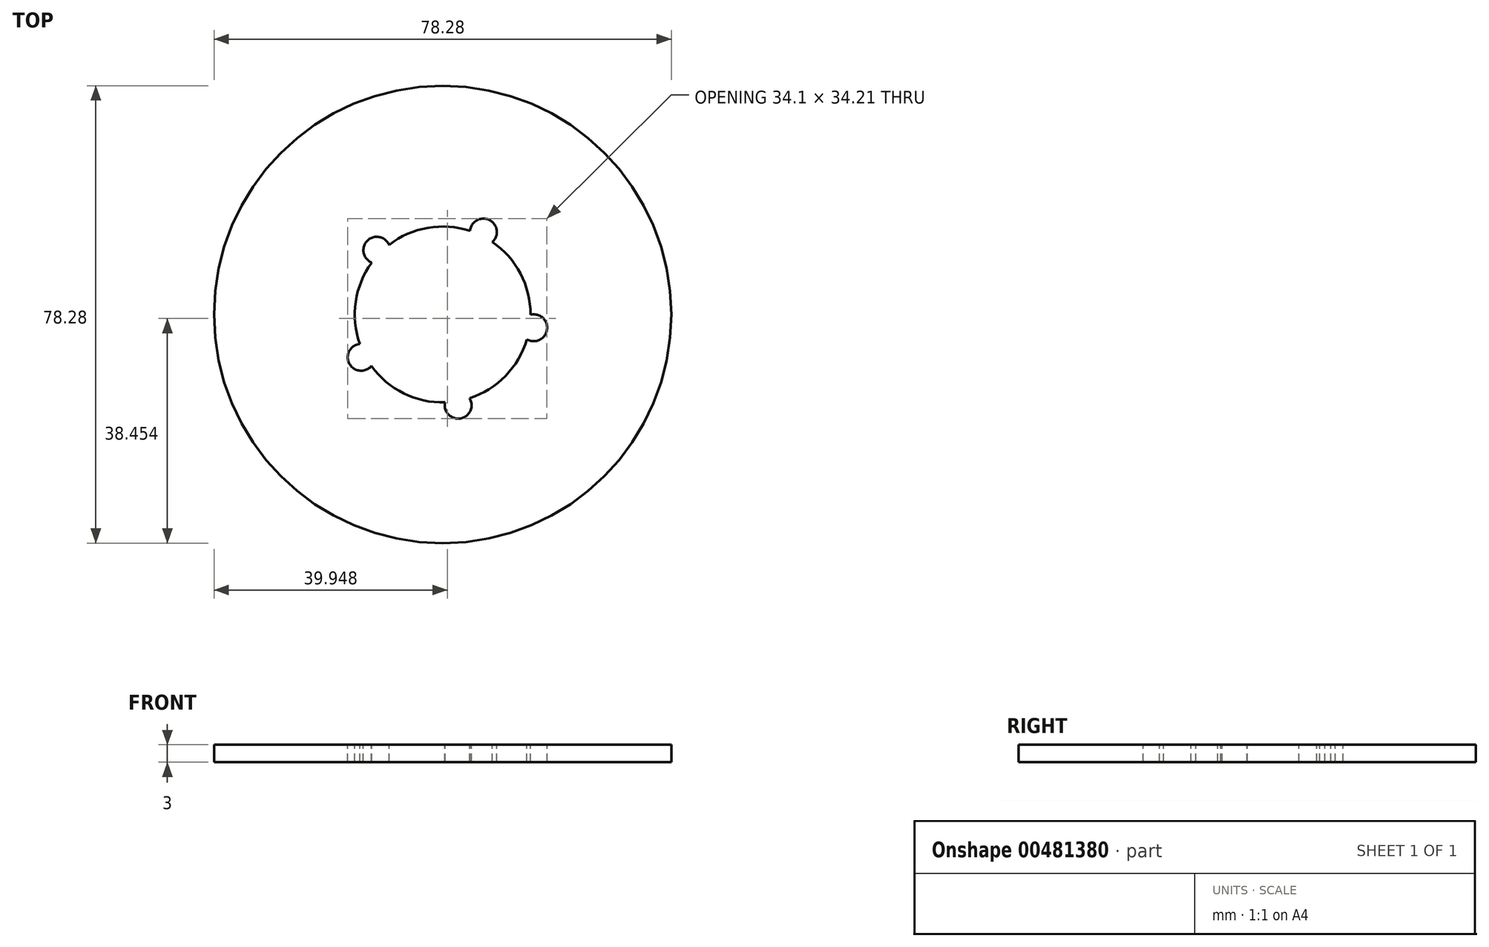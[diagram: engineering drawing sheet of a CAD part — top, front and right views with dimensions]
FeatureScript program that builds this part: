
annotation { "Feature Type Name" : "Feature", "Feature Type Description" : "" }
export const myFeature = defineFeature(function(context is Context, id is Id, definition is map)
    precondition{}
    {
        {
            var Q0;
            Q0=qCreatedBy(makeId("Top.planeOp"),FACE);
            var sketch = newSketch(context, id + "F0", { "sketchPlane" : qUnion([Q0])});
            skCircle(sketch, "E0", {"center": v(0, 0) * mm, "radius": 39.14 * mm});
            skSolve(sketch);
        }
        {
            var Q0;
            Q0 = qSketchRegion(id + "F0", true);
            extrude(context, id + "F1", {"entities" : qUnion([Q0]), "depth" : 3 * mm});
        }
        {
            var Q0;
            Q0=makeQuery(id+"F1.opExtrude","CAP_FACE",FACE,{"disambiguationData":[OSD([sQuery(id+"F0.wireOp",EDGE,"E0")])],"isStart":false});
            var sketch = newSketch(context, id + "F2", { "sketchPlane" : qUnion([Q0])});
            skCircle(sketch, "E1", {"center": v(0, 0) * mm, "radius": 15.05 * mm});
            skSolve(sketch);
        }
        {
            var Q0;
            Q0 = qSketchRegion(id + "F2", true);
            extrude(context, id + "F3", {"entities" : qUnion([Q0]), "operationType" : NewBodyOperationType.REMOVE, "oppositeDirection" : true, "depth" : 3 * mm});
        }
        {
            var Q0;
            Q0=makeQuery(id+"F1.opExtrude","CAP_FACE",FACE,{"disambiguationData":[OSD([sQuery(id+"F0.wireOp",EDGE,"E0")])],"isStart":false});
            var sketch = newSketch(context, id + "F4", { "sketchPlane" : qUnion([Q0])});
            skCircle(sketch, "E2", {"center": v(0, 0) * mm, "radius": 15.75 * mm});
            skCircle(sketch, "E3.cCircle", {"center": v(0, 0) * mm, "radius": 15.75 * mm, "construction": true});
            skLineSegment(sketch, "E3.0", {"start": v(15.59, -2.27) * mm, "end": v(2.65, -15.52) * mm});
            skLineSegment(sketch, "E3.1", {"start": v(2.65, -15.52) * mm, "end": v(-13.94, -7.32) * mm});
            skLineSegment(sketch, "E3.2", {"start": v(-13.94, -7.32) * mm, "end": v(-11.27, 11) * mm});
            skLineSegment(sketch, "E3.3", {"start": v(-11.27, 11) * mm, "end": v(6.98, 14.12) * mm});
            skLineSegment(sketch, "E3.4", {"start": v(6.98, 14.12) * mm, "end": v(15.59, -2.27) * mm});
            skCircle(sketch, "E4", {"center": v(15.59, -2.27) * mm, "radius": 2.3 * mm});
            skCircle(sketch, "E5", {"center": v(6.98, 14.12) * mm, "radius": 2.3 * mm});
            skCircle(sketch, "E6", {"center": v(2.65, -15.52) * mm, "radius": 2.3 * mm});
            skCircle(sketch, "E7", {"center": v(-13.94, -7.32) * mm, "radius": 2.3 * mm});
            skCircle(sketch, "E8", {"center": v(-11.27, 11) * mm, "radius": 2.3 * mm});
            skSolve(sketch);
        }
        {
            var Q0;
            Q0=makeQuery(id+"F4.imprint","IMPRINT",FACE,{"disambiguationData":[TD([[makeQuery(id+"F4.imprint","IMPRINT",EDGE,{"derivedFrom":makeQuery(id+"F1.opExtrude","CAP_EDGE",EDGE,{"disambiguationData":[OSD([sQuery(id+"F0.wireOp",EDGE,"E0")])],"isStart":false})}),1.0]])]});
            var sketch = newSketch(context, id + "F5", { "sketchPlane" : qUnion([Q0])});
            skCircle(sketch, "E9", {"center": v(15.58, -2.27) * mm, "radius": 2.3 * mm});
            skCircle(sketch, "E10", {"center": v(2.65, -15.52) * mm, "radius": 2.3 * mm});
            skCircle(sketch, "E11", {"center": v(-13.94, -7.32) * mm, "radius": 2.3 * mm});
            skCircle(sketch, "E12", {"center": v(-11.27, 11) * mm, "radius": 2.3 * mm});
            skCircle(sketch, "E13", {"center": v(6.98, 14.12) * mm, "radius": 2.3 * mm});
            skSolve(sketch);
        }
        {
            var Q0;
            Q0 = qSketchRegion(id + "F5", true);
            extrude(context, id + "F6", {"entities" : qUnion([Q0]), "operationType" : NewBodyOperationType.REMOVE, "oppositeDirection" : true, "depth" : 3 * mm});
        }
    });
